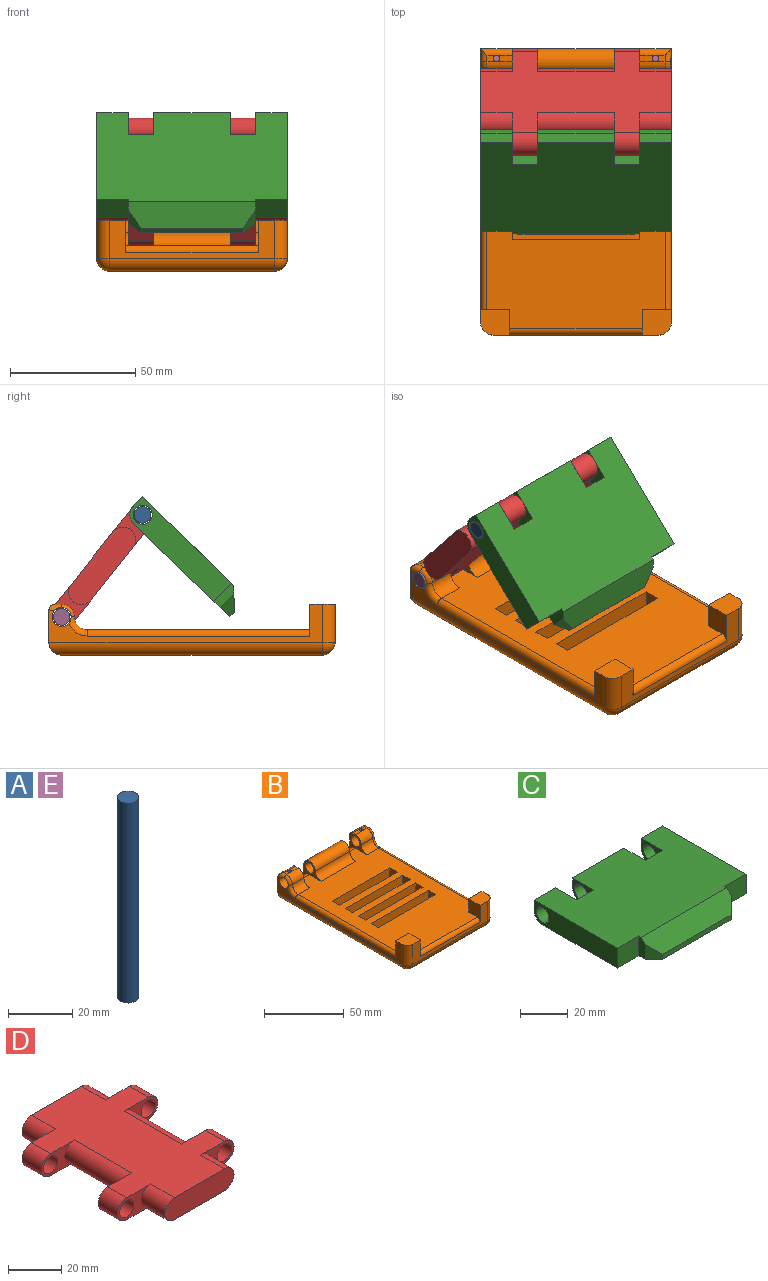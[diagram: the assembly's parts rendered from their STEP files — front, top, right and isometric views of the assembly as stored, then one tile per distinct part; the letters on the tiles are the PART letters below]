
ASSEMBLY  parts=5 mates=6
PART A: 3 faces, bbox 6.6x6.6x76.2 mm
  f0: cylinder r=3.3mm len=76.2mm, axis (0,0,-1), area 1580.9mm2, adj f1,f2
  f1: plane 6.6x6.6mm, normal (0,0,1), area 34.3mm2, adj f0
  f2: plane 6.6x6.6mm, normal (0,0,-1), area 34.3mm2, adj f0
PART B: 76 faces, bbox 76.2x114.3x20.7 mm
  f0: cylinder r=2.54mm len=88.9mm, axis (0,-1,0), area 354.7mm2, adj f1,f13,f66,f72
  f1: plane 106.68x71.12mm, normal (0,0,1), area 5641.3mm2, adj f0,f2,f15,f16,f17,f18,f20,f21
  f2: cylinder r=2.54mm len=52.83mm, axis (-1,0,0), area 210.8mm2, adj f1,f12,f68,f71
  f3: plane 6.35x2.54mm, normal (0,0,1), area 13.6mm2, adj f40,f45,f57,f60
  f4: plane 6.35x2.54mm, normal (0,0,1), area 13.6mm2, adj f37,f42,f54,f58
  f5: cylinder r=3.81mm len=12.7mm, axis (-1,0,0), area 290mm2, adj f13,f40,f56,f57,f62,f64,f66
  f6: cylinder r=3.81mm len=12.7mm, axis (-1,0,0), area 290mm2, adj f11,f37,f53,f54,f59,f61,f63
  f7: plane 12.7x12.7mm, normal (0,1,0), area 161.3mm2, adj f13,f40,f51,f60
  f8: plane 30.48x10.16mm, normal (0,1,0), area 309.7mm2, adj f36,f39,f43,f51
  f9: plane 3.81x2.54mm, normal (0,0,1), area 7.1mm2, adj f45,f57,f60,f62
  f10: plane 12.7x12.7mm, normal (0,1,0), area 161.3mm2, adj f11,f37,f51,f58
  f11: plane 109.22x15.24mm, normal (-1,0,0), area 395.8mm2, adj f6,f10,f49,f59,f63,f65,f69,f70
  f12: plane 66.04x15.24mm, normal (0,-1,0), area 335.5mm2, adj f2,f48,f68,f70,f71,f73,f74,f75
  f13: plane 109.22x15.24mm, normal (1,0,0), area 395.8mm2, adj f0,f5,f7,f50,f62,f66,f72,f73
  f14: plane 104.14x66.04mm, normal (0,0,-1), area 6877.4mm2, adj f48,f49,f50,f51
  f15: plane 50.8x8.89mm, normal (0,-1,0), area 451.6mm2, adj f1,f16,f18,f19
  f16: plane 8.89x6.35mm, normal (1,0,0), area 56.5mm2, adj f1,f15,f17,f19
  f17: plane 50.8x8.89mm, normal (0,1,0), area 451.6mm2, adj f1,f16,f18,f19
  f18: plane 8.89x6.35mm, normal (-1,0,0), area 56.5mm2, adj f1,f15,f17,f19
  f19: plane 50.8x6.35mm, normal (0,0,1), area 322.6mm2, adj f15,f16,f17,f18
  f20: plane 50.8x8.89mm, normal (0,-1,0), area 451.6mm2, adj f1,f21,f23,f24
  f21: plane 8.89x6.35mm, normal (1,0,0), area 56.5mm2, adj f1,f20,f22,f24
  f22: plane 50.8x8.89mm, normal (0,1,0), area 451.6mm2, adj f1,f21,f23,f24
  f23: plane 8.89x6.35mm, normal (-1,0,0), area 56.5mm2, adj f1,f20,f22,f24
  f24: plane 50.8x6.35mm, normal (0,0,1), area 322.6mm2, adj f20,f21,f22,f23
  f25: plane 50.8x8.89mm, normal (0,-1,0), area 451.6mm2, adj f1,f26,f28,f29
  f26: plane 8.89x6.35mm, normal (1,0,0), area 56.5mm2, adj f1,f25,f27,f29
  f27: plane 50.8x8.89mm, normal (0,1,0), area 451.6mm2, adj f1,f26,f28,f29
  f28: plane 8.89x6.35mm, normal (-1,0,0), area 56.5mm2, adj f1,f25,f27,f29
  f29: plane 50.8x6.35mm, normal (0,0,1), area 322.6mm2, adj f25,f26,f27,f28
  f30: plane 8.89x6.35mm, normal (-1,0,0), area 56.5mm2, adj f1,f31,f33,f34
  f31: plane 50.8x8.89mm, normal (0,-1,0), area 451.6mm2, adj f1,f30,f32,f34
  f32: plane 8.89x6.35mm, normal (1,0,0), area 56.5mm2, adj f1,f31,f33,f34
  f33: plane 50.8x8.89mm, normal (0,1,0), area 451.6mm2, adj f1,f30,f32,f34
  f34: plane 50.8x6.35mm, normal (0,0,1), area 322.6mm2, adj f30,f31,f32,f33
  f35: plane 3.81x2.54mm, normal (0,0,1), area 7.1mm2, adj f42,f54,f58,f59
  f36: plane 15.24x15.24mm, normal (-1,0,0), area 57.6mm2, adj f1,f8,f38,f43,f44,f51
  f37: plane 15.24x15.24mm, normal (1,0,0), area 61.8mm2, adj f1,f4,f6,f10,f41,f42,f51,f58
  f38: cylinder r=3.81mm len=30.48mm, axis (-1,0,0), area 729.7mm2, adj f36,f39
  f39: plane 15.24x15.24mm, normal (1,0,0), area 57.6mm2, adj f1,f8,f38,f43,f44,f51
  f40: plane 15.24x15.24mm, normal (-1,0,0), area 61.8mm2, adj f1,f3,f5,f7,f45,f46,f51,f60
  f41: cylinder r=5.08mm len=10.16mm, axis (-1,0,0), area 81.1mm2, adj f1,f37,f42,f63
  f42: cylinder r=5.08mm len=10.16mm, axis (1,0,0), area 81.1mm2, adj f4,f35,f37,f41,f61
  f43: cylinder r=5.08mm len=30.48mm, axis (1,0,0), area 486.4mm2, adj f8,f36,f39,f44
  f44: cylinder r=5.08mm len=30.48mm, axis (-1,0,0), area 243.2mm2, adj f1,f36,f39,f43
  f45: cylinder r=5.08mm len=10.16mm, axis (1,0,0), area 81.1mm2, adj f3,f9,f40,f46,f64
  f46: cylinder r=5.08mm len=10.16mm, axis (-1,0,0), area 81.1mm2, adj f1,f40,f45,f66
  f47: sphere r=5.08mm, area 40.5mm2, adj f48,f49,f75
  f48: cylinder r=5.08mm len=66.04mm, axis (1,0,0), area 527mm2, adj f12,f14,f47,f67
  f49: cylinder r=5.08mm len=109.22mm, axis (0,-1,0), area 856.8mm2, adj f11,f14,f47,f51
  f50: cylinder r=5.08mm len=109.22mm, axis (0,1,0), area 856.8mm2, adj f13,f14,f51,f67
  f51: cylinder r=5.08mm len=76.2mm, axis (-1,0,0), area 740.7mm2, adj f1,f7,f8,f10,f14,f36,f37,f39
  f52: cone r=0mm half-angle=59deg, axis (0,0,1), area 5.9mm2, adj f53
  f53: cylinder r=1.27mm len=4.78mm, axis (0,0,1), area 33.2mm2, adj f6,f52
  f54: cylinder r=1.27mm len=2.54mm, axis (0,0,1), area 12.9mm2, adj f4,f6,f35
  f55: cone r=0mm half-angle=59deg, axis (0,0,1), area 5.9mm2, adj f56
  f56: cylinder r=1.27mm len=4.78mm, axis (0,0,1), area 33.2mm2, adj f5,f55
  f57: cylinder r=1.27mm len=2.54mm, axis (0,0,1), area 12.9mm2, adj f3,f5,f9
  f58: cylinder r=2.54mm len=12.7mm, axis (1,0,0), area 47mm2, adj f4,f10,f35,f37,f59
  f59: cylinder r=2.54mm len=5.08mm, axis (0,1,0), area 14mm2, adj f6,f11,f35,f58,f61
  f60: cylinder r=2.54mm len=12.7mm, axis (1,0,0), area 47mm2, adj f3,f7,f9,f40,f62
  f61: torus R=2.54mm, axis (-1,0,0), area 19.4mm2, adj f6,f42,f59,f63
  f62: cylinder r=2.54mm len=5.08mm, axis (0,-1,0), area 14mm2, adj f5,f9,f13,f60,f64
  f63: torus R=7.62mm, axis (-1,0,0), area 35.5mm2, adj f6,f11,f41,f61,f65
  f64: torus R=2.54mm, axis (-1,0,0), area 19.4mm2, adj f5,f45,f62,f66
  f65: cylinder r=2.54mm len=88.9mm, axis (0,1,0), area 354.7mm2, adj f1,f11,f63,f69
  f66: torus R=7.62mm, axis (-1,0,0), area 35.5mm2, adj f0,f5,f13,f46,f64
  f67: sphere r=5.08mm, area 40.5mm2, adj f48,f50,f74
  f68: plane 12.7x10.16mm, normal (1,0,0), area 104.6mm2, adj f1,f2,f12,f69,f70
  f69: plane 12.7x11.68mm, normal (0,1,0), area 120.1mm2, adj f1,f11,f65,f68,f70
  f70: plane 11.68x10.16mm, normal (0,0,1), area 113.2mm2, adj f11,f12,f68,f69,f75
  f71: plane 12.7x10.16mm, normal (-1,0,0), area 104.6mm2, adj f1,f2,f12,f72,f73
  f72: plane 12.7x11.68mm, normal (0,1,0), area 120.1mm2, adj f0,f1,f13,f71,f73
  f73: plane 11.68x10.16mm, normal (0,0,1), area 113.2mm2, adj f12,f13,f71,f72,f74
  f74: cylinder r=5.08mm len=15.24mm, axis (0,0,-1), area 121.6mm2, adj f12,f13,f67,f73
  f75: cylinder r=5.08mm len=15.24mm, axis (0,0,1), area 121.6mm2, adj f11,f12,f47,f70
PART C: 27 faces, bbox 76.2x58.4x10.2 mm
  f0: plane 76.2x50.8mm, normal (0,0,1), area 3583.5mm2, adj f2,f3,f4,f5,f6,f7,f8,f9
  f1: plane 76.2x53.34mm, normal (0,0,-1), area 3660.9mm2, adj f4,f5,f7,f8,f9,f10,f11,f12
  f2: plane 30.48x5.08mm, normal (0,1,0), area 154.8mm2, adj f0,f9,f14,f20
  f3: plane 12.7x5.08mm, normal (0,1,0), area 64.5mm2, adj f0,f5,f11,f19
  f4: plane 49.53x10.16mm, normal (-1,0,0), area 452.1mm2, adj f0,f1,f6,f8,f21,f22
  f5: plane 49.53x10.16mm, normal (1,0,0), area 452.1mm2, adj f0,f1,f3,f16,f18,f19
  f6: plane 12.7x5.08mm, normal (0,1,0), area 64.5mm2, adj f0,f4,f12,f21
  f7: plane 10.16x3.81mm, normal (-1,0,0), area 35.5mm2, adj f0,f1,f8,f25,f26
  f8: plane 12.7x10.16mm, normal (0,-1,0), area 129mm2, adj f0,f1,f4,f7
  f9: plane 12.56x10.16mm, normal (1,0,0), area 76.5mm2, adj f0,f1,f2,f10,f17,f20
  f10: plane 10.16x10.16mm, normal (0,1,0), area 103.2mm2, adj f0,f1,f9,f11
  f11: plane 12.56x10.16mm, normal (-1,0,0), area 76.5mm2, adj f0,f1,f3,f10,f18,f19
  f12: plane 12.56x10.16mm, normal (1,0,0), area 76.5mm2, adj f0,f1,f6,f13,f21,f22
  f13: plane 10.16x10.16mm, normal (0,1,0), area 103.2mm2, adj f0,f1,f12,f14
  f14: plane 12.56x10.16mm, normal (-1,0,0), area 76.5mm2, adj f0,f1,f2,f13,f17,f20
  f15: plane 10.16x3.81mm, normal (1,0,0), area 35.5mm2, adj f0,f1,f16,f24,f26
  f16: plane 12.7x10.16mm, normal (0,-1,0), area 129mm2, adj f0,f1,f5,f15
  f17: cylinder r=3.81mm len=30.48mm, axis (-1,0,0), area 729.7mm2, adj f9,f14
  f18: cylinder r=3.81mm len=12.7mm, axis (-1,0,0), area 304mm2, adj f5,f11
  f19: cylinder r=5.08mm len=12.7mm, axis (-1,0,0), area 101.3mm2, adj f1,f3,f5,f11
  f20: cylinder r=5.08mm len=30.48mm, axis (-1,0,0), area 243.2mm2, adj f1,f2,f9,f14
  f21: cylinder r=5.08mm len=12.7mm, axis (-1,0,0), area 101.3mm2, adj f1,f4,f6,f12
  f22: cylinder r=3.81mm len=12.7mm, axis (1,0,0), area 304mm2, adj f4,f12
  f23: plane 40.64x2.54mm, normal (0,-1,0), area 103.2mm2, adj f1,f24,f25,f26
  f24: plane 7.62x5.08mm, normal (0.71,-0.71,0), area 36.5mm2, adj f1,f15,f23,f26
  f25: plane 7.62x5.08mm, normal (-0.71,-0.71,0), area 36.5mm2, adj f1,f7,f23,f26
  f26: plane 50.8x7.62mm, normal (0,-0.71,0.71), area 510.9mm2, adj f0,f7,f15,f23,f24,f25
PART D: 26 faces, bbox 62.2x76.2x10.2 mm
  f0: plane 76.2x52.07mm, normal (0,0,-1), area 2548.4mm2, adj f2,f3,f4,f5,f6,f7,f8,f9
  f1: plane 76.2x52.07mm, normal (0,0,1), area 2548.4mm2, adj f2,f3,f4,f5,f6,f7,f8,f9
  f2: plane 36.83x10.16mm, normal (0,1,0), area 352mm2, adj f0,f1,f20,f25
  f3: cylinder r=5.08mm len=10.16mm, axis (0,1,0), area 162.1mm2, adj f0,f1,f12,f14
  f4: cylinder r=5.08mm len=10.16mm, axis (0,-1,0), area 162.1mm2, adj f0,f1,f10,f11
  f5: cylinder r=5.08mm len=10.16mm, axis (0,-1,0), area 162.1mm2, adj f0,f1,f8,f9
  f6: cylinder r=5.08mm len=10.16mm, axis (0,1,0), area 162.1mm2, adj f0,f1,f13,f15
  f7: plane 36.83x10.16mm, normal (0,-1,0), area 352mm2, adj f0,f1,f22,f24
  f8: plane 17.78x10.16mm, normal (0,1,0), area 83.4mm2, adj f0,f1,f5,f18,f20
  f9: plane 17.78x10.16mm, normal (0,-1,0), area 83.4mm2, adj f0,f1,f5,f18,f21
  f10: plane 17.78x10.16mm, normal (0,1,0), area 83.4mm2, adj f0,f1,f4,f19,f21
  f11: plane 17.78x10.16mm, normal (0,-1,0), area 83.4mm2, adj f0,f1,f4,f19,f22
  f12: plane 17.78x10.16mm, normal (0,-1,0), area 83.4mm2, adj f0,f1,f3,f16,f24
  f13: plane 17.78x10.16mm, normal (0,1,0), area 83.4mm2, adj f0,f1,f6,f17,f25
  f14: plane 17.78x10.16mm, normal (0,1,0), area 83.4mm2, adj f0,f1,f3,f16,f23
  f15: plane 17.78x10.16mm, normal (0,-1,0), area 83.4mm2, adj f0,f1,f6,f17,f23
  f16: cylinder r=3.81mm len=10.16mm, axis (0,-1,0), area 243.2mm2, adj f12,f14
  f17: cylinder r=3.81mm len=10.16mm, axis (0,-1,0), area 243.2mm2, adj f13,f15
  f18: cylinder r=3.81mm len=10.16mm, axis (0,-1,0), area 243.2mm2, adj f8,f9
  f19: cylinder r=3.81mm len=10.16mm, axis (0,-1,0), area 243.2mm2, adj f10,f11
  f20: cylinder r=5.08mm len=12.7mm, axis (0,1,0), area 202.7mm2, adj f0,f1,f2,f8
  f21: cylinder r=5.08mm len=30.48mm, axis (0,1,0), area 486.4mm2, adj f0,f1,f9,f10
  f22: cylinder r=5.08mm len=12.7mm, axis (0,1,0), area 202.7mm2, adj f0,f1,f7,f11
  f23: cylinder r=5.08mm len=30.48mm, axis (0,-1,0), area 486.4mm2, adj f0,f1,f14,f15
  f24: cylinder r=5.08mm len=12.7mm, axis (0,-1,0), area 202.7mm2, adj f0,f1,f7,f12
  f25: cylinder r=5.08mm len=12.7mm, axis (0,-1,0), area 202.7mm2, adj f0,f1,f2,f13
PART E: same geometry as A
PLACE A rot(axis=(0.35,-0.87,-0.35),98.1deg) t=(51.24,64.8,142.94)mm
PLACE B t=(-24.96,-22.46,9.7)mm fixed
PLACE C rot(axis=(1,0,0),44deg) t=(-24.96,18.68,24.12)mm
PLACE D rot(axis=(-0.4,-0.4,-0.83),100.9deg) t=(-24.96,85.94,17.81)mm
PLACE E rot(axis=(0,-1,0),90deg) t=(51.24,147.91,73.2)mm
MATE revolute E.f0 <-> D.f3  axis (1,0,0) through (13.14,86.76,24.94)mm
MATE planar E.f0 <-> B.f5  axis (1,0,0) through (51.24,86.76,24.94)mm
MATE slider C.f22 <-> A.f0  axis (-1,0,0) through (51.24,54.4,65.73)mm
MATE slider E.f0 <-> B.f5  axis (1,0,0) through (51.24,86.76,24.94)mm
MATE fastened A.f0 <-> C.f22  axis (1,0,0) through (51.24,54.4,65.73)mm
MATE revolute D.f18 <-> C.f22  axis (1,0,0) through (38.54,54.4,65.73)mm
